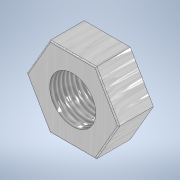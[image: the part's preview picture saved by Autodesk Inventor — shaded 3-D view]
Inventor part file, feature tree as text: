
AUTODESK INVENTOR PART (.ipt)
format: ipt  version: 2021 (Build 250183000, 183)  size: 123,392 bytes
history: native  units: mm
features: other x1, extrude x1, fillet x1, thread x1, sketch x1
ambient origin geometry x8: Origin, YZ Plane, XZ Plane, XY Plane, X Axis, Y Axis, Z Axis, Center Point
bodies: Body1 (feature_tree)
feature tree (5):
  other  "Sólido1"
  extrude  "Extrusão1"  Depth=8.0mm
  fillet  "Arredondamento1"  Radius=6.0mm
  thread  "Rosca1"  [1 undecoded]
  sketch  "Esboço1"  dims[d0=8.0mm d1=8.0mm d2=6.0mm d3=0.0mm d4=0.2mm d5=7.0mm d6=0.0mm]
note: 1 required parameter value undecoded (feature->parameter linkage not recoverable at this tier; creation-order binding heuristic only, values carry confidence <= 0.55)
